FCSTD DOCUMENT  (FreeCAD 0.14R3637 (Git))
Label: Vexta_motor_just_holes
License: CC-BY 3.0
LicenseURL: http://creativecommons.org/licenses/by/3.0/
objects: Sketcher::SketchObject×1
note: 1 computed .brp shape members not serialized (recipe doc carries the construction recipe); baked Part::Feature solids carry a one-line shape summary decoded from their .brp

FEATURE [Sketcher::SketchObject] Sketch005  label="Parametrized side holes"
  Placement = pos=(2.365,0,0) rot=(0.57735,-0.57735,-0.57735;2.0944rad)
  sketch-geometry (28):
    g0: LineSegment [constr] StartX=18.7556 StartY=3.40339 StartZ=0 EndX=26.2479 EndY=3.40339 EndZ=0
    g1: LineSegment [constr] StartX=26.2479 StartY=3.40339 StartZ=0 EndX=26.2479 EndY=-8.02336 EndZ=0
    g2: LineSegment [constr] StartX=26.2479 StartY=-8.02336 StartZ=0 EndX=18.7556 EndY=-8.02336 EndZ=0
    g3: LineSegment [constr] StartX=18.7556 StartY=-8.02336 StartZ=0 EndX=18.7556 EndY=3.40339 EndZ=0
    g4: Circle CenterX=18.7556 CenterY=3.40339 CenterZ=0 NormalX=0 NormalY=0 NormalZ=1 Radius=1.5
    g5: Circle CenterX=26.2479 CenterY=3.40339 CenterZ=0 NormalX=0 NormalY=0 NormalZ=1 Radius=1.5
    g6: Circle CenterX=18.7556 CenterY=-8.02336 CenterZ=0 NormalX=0 NormalY=0 NormalZ=1 Radius=1.5
    g7: Circle CenterX=26.2479 CenterY=-8.02336 CenterZ=0 NormalX=0 NormalY=0 NormalZ=1 Radius=1.5
    g8: Circle [constr] CenterX=22.5017 CenterY=-2.30999 CenterZ=0 NormalX=0 NormalY=0 NormalZ=1 Radius=6.83201
    g9: Circle [constr] CenterX=22.5017 CenterY=-2.30999 CenterZ=0 NormalX=0 NormalY=0 NormalZ=1 Radius=13.664
    g10: LineSegment [constr] StartX=15.0094 StartY=9.11677 StartZ=0 EndX=29.994 EndY=9.11677 EndZ=0
    g11: LineSegment [constr] StartX=29.994 StartY=9.11677 StartZ=0 EndX=29.994 EndY=-13.7367 EndZ=0
    g12: LineSegment [constr] StartX=29.994 StartY=-13.7367 StartZ=0 EndX=15.0094 EndY=-13.7367 EndZ=0
    g13: LineSegment [constr] StartX=15.0094 StartY=-13.7367 StartZ=0 EndX=15.0094 EndY=9.11677 EndZ=0
    g14: Circle [constr] CenterX=18.7556 CenterY=-2.30999 CenterZ=0 NormalX=0 NormalY=0 NormalZ=1 Radius=5.71338
    g15: Circle [constr] CenterX=26.2479 CenterY=-2.30999 CenterZ=0 NormalX=0 NormalY=0 NormalZ=1 Radius=5.71338
    g16: Circle [constr] CenterX=15.0094 CenterY=-2.30999 CenterZ=0 NormalX=0 NormalY=0 NormalZ=1 Radius=11.4268
    g17: LineSegment [constr] StartX=15.0094 StartY=-2.30999 StartZ=0 EndX=18.7556 EndY=-2.30999 EndZ=0
    g18: Circle [constr] CenterX=29.994 CenterY=-2.30999 CenterZ=0 NormalX=0 NormalY=0 NormalZ=1 Radius=11.4268
    g19: LineSegment [constr] StartX=18.7556 StartY=-2.30999 StartZ=0 EndX=22.5017 EndY=-2.30999 EndZ=0
    g20: Circle [constr] CenterX=22.5017 CenterY=3.40339 CenterZ=0 NormalX=0 NormalY=0 NormalZ=1 Radius=3.74615
    g21: Circle [constr] CenterX=22.5017 CenterY=9.11677 CenterZ=0 NormalX=0 NormalY=0 NormalZ=1 Radius=7.4923
    g22: LineSegment [constr] StartX=22.5017 StartY=9.11677 StartZ=0 EndX=22.5017 EndY=3.40339 EndZ=0
    g23: LineSegment [constr] StartX=22.5017 StartY=-2.30999 StartZ=0 EndX=22.5017 EndY=3.40339 EndZ=0
    g24: LineSegment StartX=-60.86 StartY=9.11677 StartZ=0 EndX=29.994 EndY=9.11677 EndZ=0
    g25: LineSegment StartX=29.994 StartY=9.11677 StartZ=0 EndX=29.994 EndY=-13.7367 EndZ=0
    g26: LineSegment StartX=29.994 StartY=-13.7367 StartZ=0 EndX=-60.86 EndY=-13.7367 EndZ=0
    g27: LineSegment StartX=-60.86 StartY=-13.7367 StartZ=0 EndX=-60.86 EndY=9.11677 EndZ=0
  constraints (70):
    c: Coincident(g0,g1)
    c: Coincident(g1,g2)
    c: Coincident(g2,g3)
    c: Coincident(g3,g0)
    c: Horizontal(g0)
    c: Horizontal(g2)
    c: Vertical(g1)
    c: Vertical(g3)
    c: Coincident(g4,g0)
    c: Coincident(g5,g0)
    c: Coincident(g6,g2)
    c: Coincident(g7,g1)
    c: Equal(g4,g5)
    c: Equal(g5,g7)
    c: Equal(g7,g6)
    c: PointOnObject(g0,g8)
    c: PointOnObject(g0,g8)
    c: PointOnObject(g1,g8)
    c: Coincident(g9,g8)
    c: Coincident(g10,g11)
    c: Coincident(g11,g12)
    c: Coincident(g12,g13)
    c: Coincident(g13,g10)
    c: Horizontal(g10)
    c: Horizontal(g12)
    c: Vertical(g11)
    c: Vertical(g13)
    c: PointOnObject(g10,g9)
    c: PointOnObject(g12,g9)
    c: PointOnObject(g11,g9)
    c: Radius(g5) = 1.5
    c: PointOnObject(g14,g3)
    c: PointOnObject(g0,g14)
    c: PointOnObject(g2,g14)
    c: PointOnObject(g15,g1)
    c: PointOnObject(g0,g15)
    c: PointOnObject(g1,g15)
    c: PointOnObject(g16,g13)
    c: PointOnObject(g10,g16)
    c: PointOnObject(g12,g16)
    c: Coincident(g17,g16)
    c: Coincident(g17,g14)
    c: PointOnObject(g18,g11)
    c: PointOnObject(g10,g18)
    c: PointOnObject(g11,g18)
    c: Coincident(g19,g14)
    c: Coincident(g19,g8)
    c: Equal(g17,g19)
    c: PointOnObject(g20,g0)
    c: PointOnObject(g0,g20)
    c: PointOnObject(g0,g20)
    c: PointOnObject(g21,g10)
    c: PointOnObject(g10,g21)
    c: PointOnObject(g10,g21)
    c: Coincident(g22,g21)
    c: Coincident(g22,g20)
    c: Coincident(g23,g8)
    c: Coincident(g23,g20)
    c: Equal(g22,g23)
    c: DistanceY(g10) = 0
    c: Coincident(g24,g25)
    c: Coincident(g25,g26)
    c: Coincident(g26,g27)
    c: Coincident(g27,g24)
    c: Horizontal(g24)
    c: Horizontal(g26)
    c: Vertical(g25)
    c: Vertical(g27)
    c: Coincident(g25,g11)
    c: Coincident(g24,g10)
